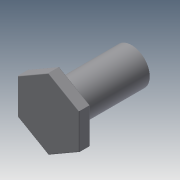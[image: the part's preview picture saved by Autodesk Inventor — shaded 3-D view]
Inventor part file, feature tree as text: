
AUTODESK INVENTOR PART (.ipt)
format: ipt  version: 2015 (Build 190159000, 159)  size: 111,104 bytes
history: native  units: mm
features: extrude x2, fillet x2, sketch x2
ambient origin geometry x8: Origin, YZ Plane, XZ Plane, XY Plane, X Axis, Y Axis, Z Axis, Center Point
bodies: Solid1 (feature_tree)
feature tree (6):
  extrude  "Extrusion1"  Depth=3.0mm
  extrude  "Extrusion2"  Depth=20.0mm TaperAngle=0.0deg
  fillet  "Fillet1"  Radius=0.2mm
  fillet  "Fillet2"  Radius=1.0mm
  sketch  "Sketch1"  dims[d1=3.0mm d2=0.0mm d3=19.6mm]
  sketch  "Sketch2"  dims[d4=10.0mm d5=20.0mm d6=0.0mm d7=0.2mm d8=1.0mm]
